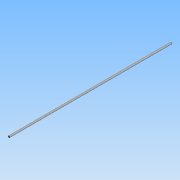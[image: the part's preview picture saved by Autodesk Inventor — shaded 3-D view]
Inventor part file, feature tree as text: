
AUTODESK INVENTOR PART (.ipt)
format: ipt  version: 2015 (Build 190159000, 159)  size: 64,512 bytes
history: native  units: mm
features: extrude x1, sketch x1
ambient origin geometry x8: Origin, YZ Plane, XZ Plane, XY Plane, X Axis, Y Axis, Z Axis, Center Point
bodies: Solid1 (feature_tree)
feature tree (2):
  extrude  "Extrusion1"  Depth=410.0mm TaperAngle=0.0deg
  sketch  "Sketch1"  dims[d0=5.0mm d1=410.0mm d2=0.0mm]
